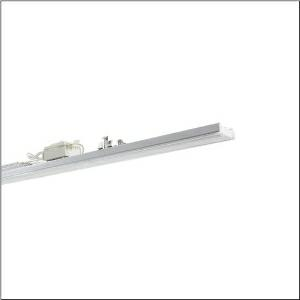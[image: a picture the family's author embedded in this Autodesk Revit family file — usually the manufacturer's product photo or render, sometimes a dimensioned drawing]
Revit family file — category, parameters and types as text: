
# Revit family: licross_11_recessed_mo_51tl12dv455g
name_source: partatom
category: Lighting Fixtures
units: mm (PartAtom-declared; Revit-internal decimal feet)

## family parameters
Cut with Voids When Loaded = No
Host = Face
Light Source = No
Part Type = Normal
Room Calculation Point = No
Round Connector Dimension = Use Diameter
Shared = No

## types (1)
- --- (1 x LED, 5700 lm, 29.1 W, 4000K)
    Apparent Load = 29 VA
    CIE Flux Codes = 67 92 99 100 100
    Color Rendering = 80
    Color Temperature = 4000K
    Default Elevation = 1800 mm
    Description = Licross 11 Recessed MO, luminaire insert, of sheet steel, coil coated, white, length: 2.250mm, width: 66mm, height: 67mm, LED rated luminous flux: 5.700lm, light colour: 840, SDCM (Standard Deviation of Colour Matching)MacAdam ≤ 2 SDCM (initial), control gear: DALI 2, with plug, 5-pole, with phase selection, mains connection: 220..240V, AC, 50/60Hz, rated input power: 29W, internal wiring halogen-free, primary optical cover: cover, of PMMA, light emission: direct distribution, primary light characteristic: symmetric, protection rating (complete): IP40, insulation class (complete): insulation class I (protective earthing), certification: CE, ENEC, VDE, UKCA, protection symbol: D if used in an environment without relevant dust loads with corresponding accessories, impact resistance: IK06, permissible ambient temperature for indoor applications: -25..+45°C, corresponds to IFS (International Featured Standards) requirements for safety and quality in the food industry, reducing of maximum allowable ambient temperature of 5°C with ceiling mounting, LABS conformity tested according to VDMA 24364:2018-05, The light source and the operating device comply with the requirements of the Ecodesign Regulation (EU) 2019/2020 and are replaceable in accordance with this regulation, packaging unit: 1 piece
    Height = 58 mm
    Lamp = 1 x LED
    Lamp Light Flux = 5700 lm
    Lamp Power = 29.1 W
    Lamp count = 1
    Length = 2250 mm
    Luminous efficacy = 196 lm/W
    Manufacturer = Siteco
    ModVariant = No
    Model = 51TL12DV455G
    Mounting Place = Ceiling
    Mounting Type = Pendant
    Number of Poles = 1
    OnlyDefault = Yes
    Power Factor = 1
    Product Name = Licross 11 Recessed MO
    Product group = luminaire insert | ceiling pendant
    ProductGroupID = 901
    Protection Class = Protection class I
    Protection Degree = IP 40
    RLX_Detail_Level = 1
    RLX_Emergency_Light_Flux = 0 lm
    RLX_Emergency_Type = 0
    RLX_Emergency_Type_DB = No
    RlxData = <blob elided: 29485 chars, md5=287c3869>
    Socket = socket
    Standby Power = 0 W
    System Light Flux = 5700 lm
    System Power = 29 W
    Type Comments = factory setting: luminous flux: 100 % | dim-lin: 254 | 133 mA
    Type Image = l_1296930.jpg
    URL = http://relux.com
    VarID = @adj_101933
    Voltage = 0 V
    Weight = 0.00 kg
    Width = 66 mm

## geometry (parser evidence)
native form markers: Blend x4, Sweep x9
no freeform markers — native parametric forms only
